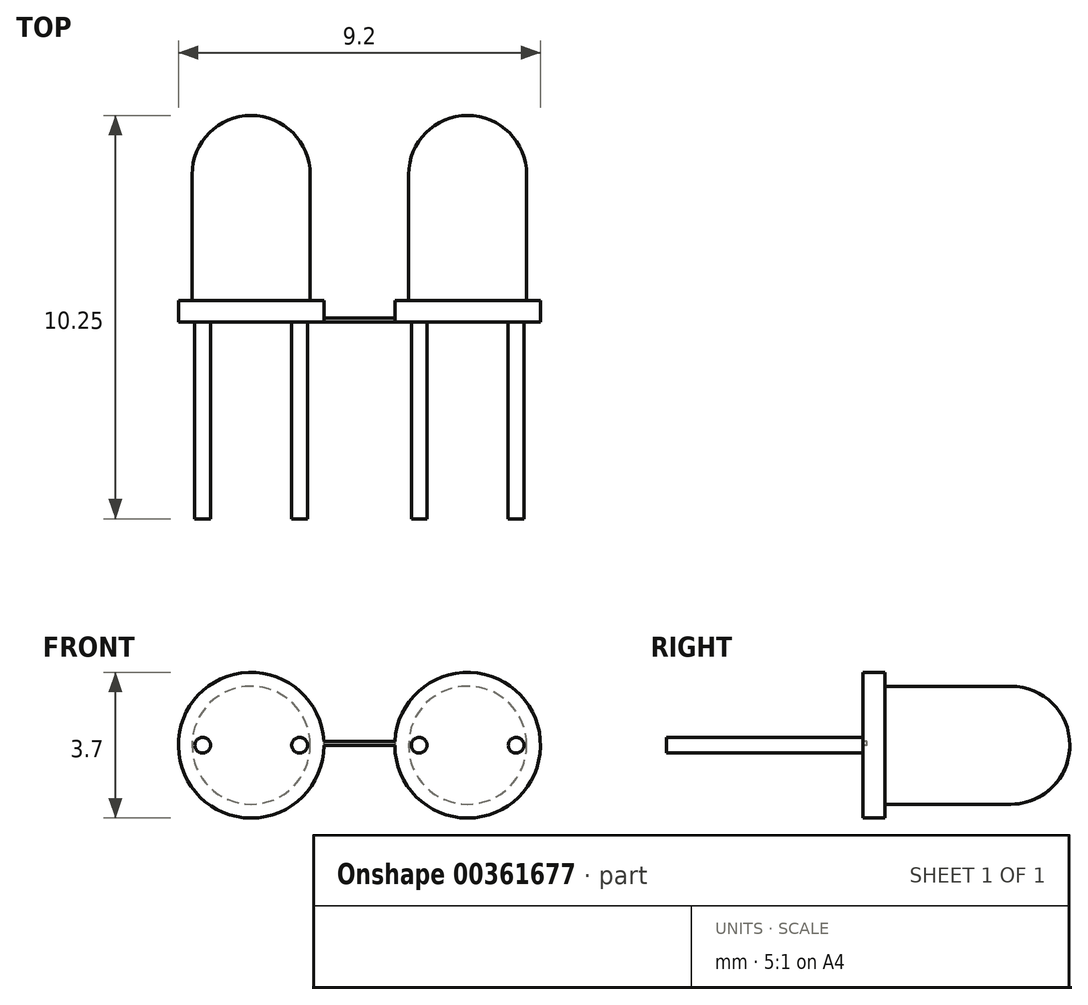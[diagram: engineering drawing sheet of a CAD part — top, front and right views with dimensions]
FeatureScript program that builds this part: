
annotation { "Feature Type Name" : "Feature", "Feature Type Description" : "" }
export const myFeature = defineFeature(function(context is Context, id is Id, definition is map)
    precondition{}
    {
        {
            var Q0;
            Q0=qCreatedBy(makeId("Top.planeOp"),FACE);
            var sketch = newSketch(context, id + "F0", { "sketchPlane" : qUnion([Q0])});
            skLineSegment(sketch, "E0.bottom", {"start": v(-2.75, 3.32) * mm, "end": v(-1.25, 3.32) * mm});
            skLineSegment(sketch, "E0.top", {"start": v(-2.75, -1.93) * mm, "end": v(-1.25, -1.93) * mm});
            skLineSegment(sketch, "E0.right", {"start": v(-1.25, 3.32) * mm, "end": v(-1.25, -1.38) * mm});
            skLineSegment(sketch, "E1", {"start": v(-2.75, -1.93) * mm, "end": v(-2.75, 6.15) * mm});
            skLineSegment(sketch, "E2.right", {"start": v(-0.9, -1.93) * mm, "end": v(-0.9, -1.38) * mm});
            skLineSegment(sketch, "E3", {"start": v(-1.25, -1.93) * mm, "end": v(-0.9, -1.93) * mm});
            skLineSegment(sketch, "E4.trimOffspring", {"start": v(-1.25, -1.38) * mm, "end": v(-0.9, -1.38) * mm});
            skSolve(sketch);
        }
        {
            var Q0;
            {var subQ1=sQuery(id+"F0.wireOp",EDGE,"E0.bottom");Q0=makeQuery(id+"F0.imprint","IMPRINT",FACE,{"disambiguationData":[TD([[makeQuery(id+"F0.imprint","IMPRINT",EDGE,{"derivedFrom":subQ1}),-1.0]])]});}
            var Q1;
            Q1=sQuery(id+"F0.wireOp",EDGE,"E1");
            revolve(context, id + "F1", {"entities" : qUnion([Q0]), "axis" : qUnion([Q1]), "revolveType" : RevolveType.FULL});
        }
        {
            var Q0;
            Q0=makeQuery(id+"F1.opRevolve","SWEPT_EDGE",EDGE,{"disambiguationData":[OSD([sQuery(id+"F0.wireOp",EDGE,"E0.bottom"),sQuery(id+"F0.wireOp",EDGE,"E0.right")])]});
            fillet(context, id + "F2", {"entities" : qUnion([Q0]), "radius" : 1.5 * mm, "tangentPropagation" : true, "allowEdgeOverflow" : false});
        }
        {
            var Q0;
            Q0=makeQuery(id+"F1.opRevolve","SWEPT_FACE",FACE,{"disambiguationData":[OSD([sQuery(id+"F0.wireOp",EDGE,"E0.top"),sQuery(id+"F0.wireOp",EDGE,"E3")])]});
            var sketch = newSketch(context, id + "F3", { "sketchPlane" : qUnion([Q0])});
            skPoint(sketch, "E5", {"position": v(-3.98, 0) * mm});
            skPoint(sketch, "E6", {"position": v(-1.52, 0) * mm});
            skLineSegment(sketch, "E7", {"start": v(-3.98, 0) * mm, "end": v(-4.6, 0) * mm, "construction": true});
            skLineSegment(sketch, "E8", {"start": v(-1.52, 0) * mm, "end": v(-0.9, 0) * mm, "construction": true});
            skCircle(sketch, "E9", {"center": v(-3.98, 0) * mm, "radius": 0.2 * mm});
            skCircle(sketch, "E10", {"center": v(-1.52, 0) * mm, "radius": 0.2 * mm});
            skLineSegment(sketch, "E11.bottom", {"start": v(-0.9, 0.1) * mm, "end": v(4.1, 0.1) * mm});
            skLineSegment(sketch, "E11.top", {"start": v(-0.9, 0) * mm, "end": v(4.1, 0) * mm});
            skLineSegment(sketch, "E11.left", {"start": v(-0.9, 0.1) * mm, "end": v(-0.9, 0) * mm});
            skLineSegment(sketch, "E11.right", {"start": v(4.1, 0.1) * mm, "end": v(4.1, 0) * mm});
            skSolve(sketch);
        }
        {
            var Q0;
            Q0=makeQuery(id+"F3.imprint","IMPRINT",FACE,{"disambiguationData":[TD([[makeQuery(id+"F3.imprint","IMPRINT",EDGE,{"derivedFrom":sQuery(id+"F3.wireOp",EDGE,"E10")}),1.0]])]});
            var Q1;
            Q1=makeQuery(id+"F3.imprint","IMPRINT",FACE,{"disambiguationData":[TD([[makeQuery(id+"F3.imprint","IMPRINT",EDGE,{"derivedFrom":sQuery(id+"F3.wireOp",EDGE,"E9")}),1.0]])]});
            extrude(context, id + "F4", {"entities" : qUnion([Q0, Q1]), "operationType" : NewBodyOperationType.ADD, "depth" : 5 * mm});
        }
        {
            var Q0;
            Q0=makeQuery(id+"F1.opRevolve","SWEPT_BODY",BODY,{"disambiguationData":[OSD([sQuery(id+"F0.wireOp",EDGE,"E0.bottom"),sQuery(id+"F0.wireOp",EDGE,"E0.right"),sQuery(id+"F0.wireOp",EDGE,"E1"),sQuery(id+"F0.wireOp",EDGE,"E2.right"),sQuery(id+"F0.wireOp",EDGE,"E0.top"),sQuery(id+"F0.wireOp",EDGE,"E3"),sQuery(id+"F0.wireOp",EDGE,"E4.trimOffspring")])]});
            var Q1;
            Q1=qCreatedBy(makeId("Right.planeOp"),FACE);
            mirror(context, id + "F5", {"entities" : qUnion([Q0]), "mirrorPlane" : qUnion([Q1])});
        }
        {
            var Q0;
            {var subQ0=sQuery(id+"F3.wireOp",EDGE,"E11.bottom");Q0=makeQuery(id+"F3.imprint","IMPRINT",FACE,{"disambiguationData":[TD([[makeQuery(id+"F3.imprint","IMPRINT",EDGE,{"derivedFrom":subQ0}),-1.0]])]});}
            extrude(context, id + "F6", {"entities" : qUnion([Q0]), "operationType" : NewBodyOperationType.ADD, "oppositeDirection" : true, "depth" : 0.1 * mm});
        }
    });
